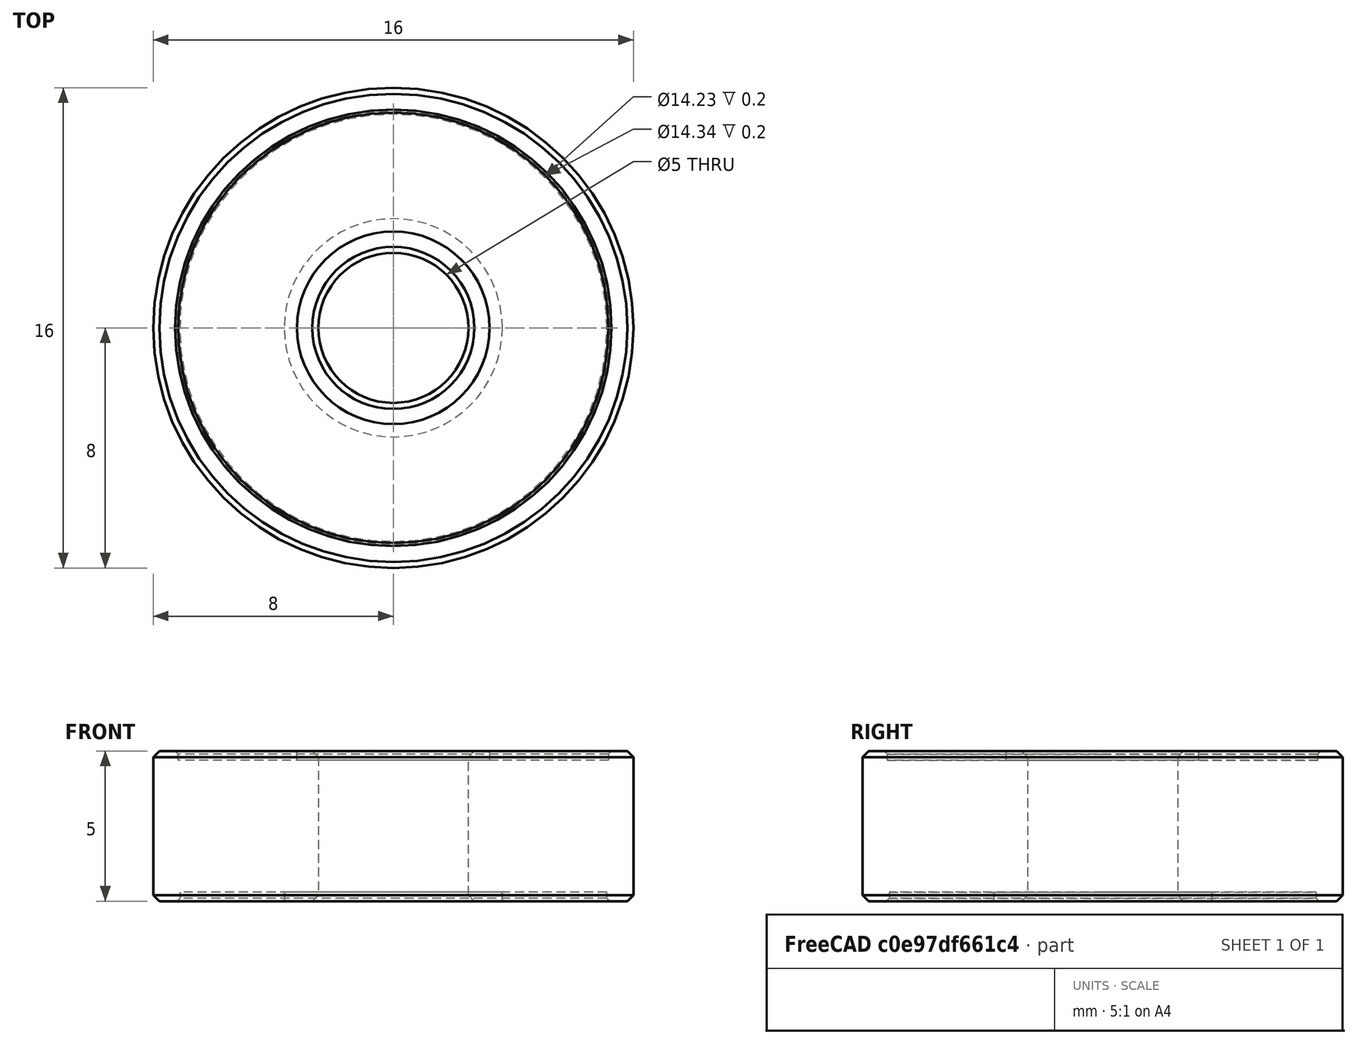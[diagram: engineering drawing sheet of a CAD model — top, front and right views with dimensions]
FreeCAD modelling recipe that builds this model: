
FCSTD DOCUMENT  (FreeCAD 0.21R30669 (Git))
Label: bearing_16x5x5
License: All rights reserved
LicenseURL: http://en.wikipedia.org/wiki/All_rights_reserved
objects: PartDesign::Chamfer×2, Sketcher::SketchObject×2, PartDesign::Pocket×2, PartDesign::AdditiveCylinder×1, PartDesign::SubtractiveCylinder×1, PartDesign::Body×1
note: 15 computed .brp shape members not serialized (recipe doc carries the construction recipe); baked Part::Feature solids carry a one-line shape summary decoded from their .brp

FEATURE [PartDesign::AdditiveCylinder] Cylinder
  Angle = 360
  AttacherType = Attacher::AttachEngine3D
  FirstAngle = 0
  Height = 5
  Radius = 8
  SecondAngle = 0
FEATURE [PartDesign::SubtractiveCylinder] Cylinder001
  Angle = 360
  AttacherType = Attacher::AttachEngine3D
  BaseFeature = -> Cylinder
  FirstAngle = 0
  Height = 10
  Radius = 2.5
  SecondAngle = 0
FEATURE [PartDesign::Chamfer] Chamfer
  Angle = 45
  Base = -> Cylinder001 [Edge3,Edge2,Edge5,Edge4]
  BaseFeature = -> Cylinder001
  ChamferType = 0
  FlipDirection = false
  Size = 0.2
  Size2 = 1
  SupportTransform = false
  UseAllEdges = false
FEATURE [Sketcher::SketchObject] Sketch
  FullyConstrained = false
  MapMode = 5
  Placement = pos=(0,0,5) rot=(0,0,1;0rad)
  Support = -> [Chamfer]
  sketch-geometry (2):
    g0: Circle CenterX=0 CenterY=0 CenterZ=0 NormalX=0 NormalY=0 NormalZ=1 AngleXU=0 Radius=3.2082
    g1: Circle CenterX=0 CenterY=0 CenterZ=0 NormalX=0 NormalY=0 NormalZ=1 AngleXU=0 Radius=7.17148
  constraints (2):
    c: Coincident(g0,g-1)
    c: Coincident(g1,g0)
FEATURE [PartDesign::Pocket] Pocket
  BaseFeature = -> Chamfer
  Direction = (0,0,-1)
  Length = 0.3
  Length2 = 5
  Profile = -> Sketch
  ReferenceAxis = -> Sketch [N_Axis]
  Type = 0
FEATURE [Sketcher::SketchObject] Sketch001
  FullyConstrained = false
  MapMode = 5
  Placement = pos=(0,0,0) rot=(1,0,0;3.14159rad)
  Support = -> [Pocket]
  sketch-geometry (2):
    g0: Circle CenterX=0 CenterY=0 CenterZ=0 NormalX=0 NormalY=0 NormalZ=1 AngleXU=0 Radius=3.63459
    g1: Circle CenterX=0 CenterY=0 CenterZ=0 NormalX=0 NormalY=0 NormalZ=1 AngleXU=0 Radius=7.11429
  constraints (2):
    c: Coincident(g0,g-1)
    c: Coincident(g1,g0)
FEATURE [PartDesign::Pocket] Pocket001
  BaseFeature = -> Pocket
  Direction = (0,0,1)
  Length = 0.3
  Length2 = 5
  Profile = -> Sketch001
  ReferenceAxis = -> Sketch001 [N_Axis]
  Type = 0
FEATURE [PartDesign::Chamfer] Chamfer001
  Angle = 45
  Base = -> Pocket001 [Edge9,Edge8]
  BaseFeature = -> Pocket001
  ChamferType = 0
  FlipDirection = false
  Size = 0.1
  Size2 = 1
  SupportTransform = false
  UseAllEdges = false
FEATURE [PartDesign::Body] Body
  Group = -> [Cylinder,Cylinder001,Chamfer,Sketch,Pocket,Sketch001,Pocket001,Chamfer001]
  Origin = -> Origin
  Tip = -> Chamfer001
